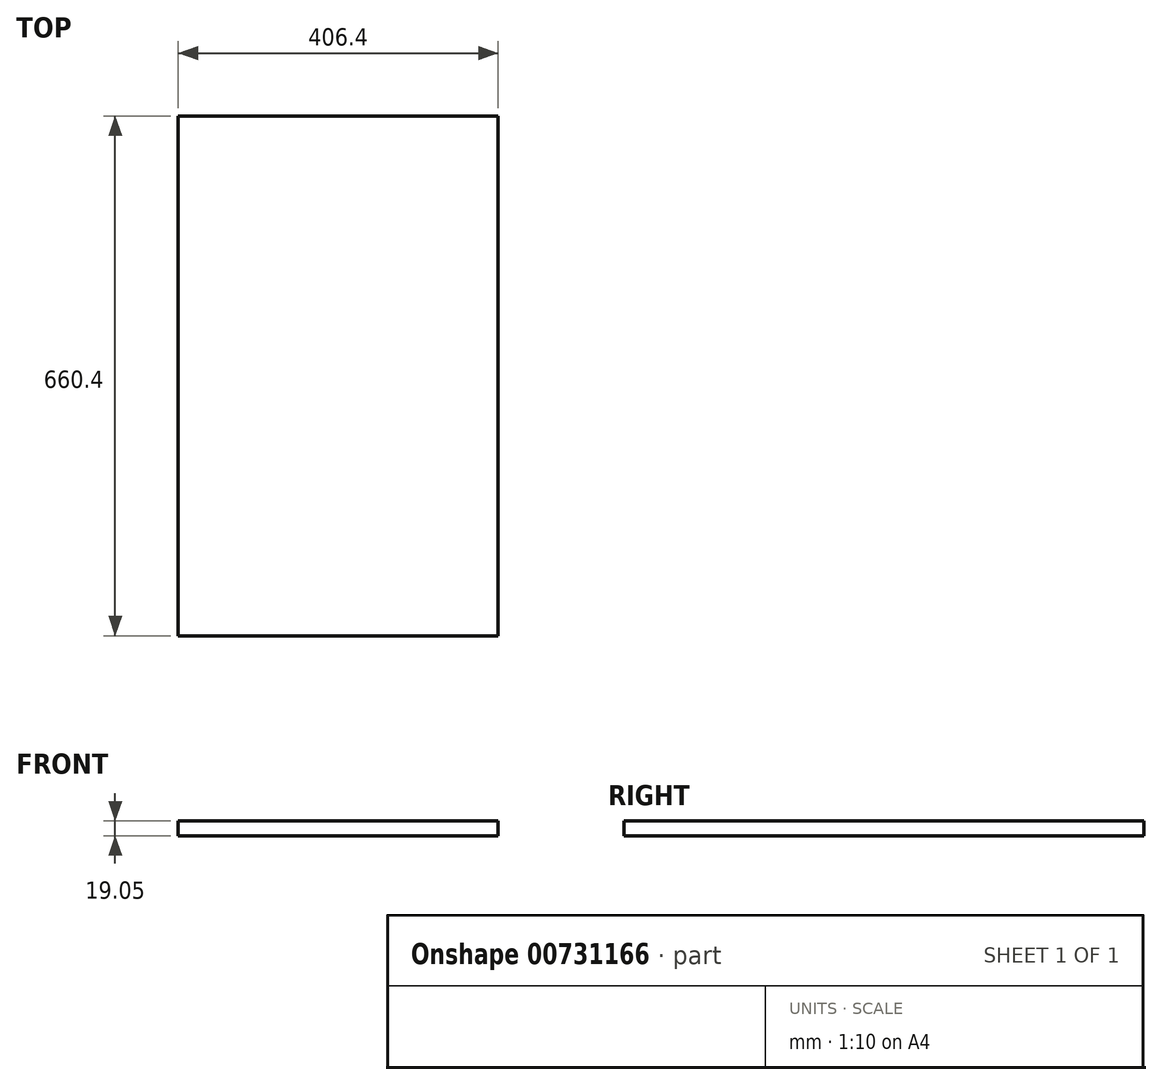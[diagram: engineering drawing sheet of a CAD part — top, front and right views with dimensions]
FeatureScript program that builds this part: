
annotation { "Feature Type Name" : "Feature", "Feature Type Description" : "" }
export const myFeature = defineFeature(function(context is Context, id is Id, definition is map)
    precondition{}
    {
        {
            var Q0;
            Q0=qCreatedBy(makeId("Top.planeOp"),FACE);
            var sketch = newSketch(context, id + "F0", { "sketchPlane" : qUnion([Q0])});
            skLineSegment(sketch, "E0.bottom", {"start": v(203.2, 330.2) * mm, "end": v(-203.2, 330.2) * mm});
            skLineSegment(sketch, "E0.top", {"start": v(203.2, -330.2) * mm, "end": v(-203.2, -330.2) * mm});
            skLineSegment(sketch, "E0.left", {"start": v(203.2, 330.2) * mm, "end": v(203.2, -330.2) * mm});
            skLineSegment(sketch, "E0.right", {"start": v(-203.2, 330.2) * mm, "end": v(-203.2, -330.2) * mm});
            skPoint(sketch, "E0.middle", {"position": v(0, 0) * mm});
            skSolve(sketch);
        }
        {
            var Q0;
            Q0 = qSketchRegion(id + "F0", true);
            extrude(context, id + "F1", {"entities" : qUnion([Q0]), "depth" : 19.05 * mm, "offsetDistance" : 25.4 * mm});
        }
    });
